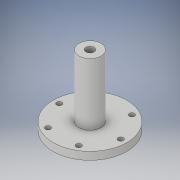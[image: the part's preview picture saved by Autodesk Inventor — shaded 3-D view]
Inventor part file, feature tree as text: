
AUTODESK INVENTOR PART (.ipt)
format: ipt  version: 2017 (Build 210142000, 142)  size: 154,624 bytes
history: native  units: in
note: dims shown in document units (in); Inventor stores cm internally (conversion verified against a paired STEP export)
features: sketch x4, hole x2, pattern_circular x2, revolve x1
ambient origin geometry x8: Origin, YZ Plane, XZ Plane, XY Plane, X Axis, Y Axis, Z Axis, Center Point
bodies: Solid1 (feature_tree)
feature tree (9):
  revolve  "Revolution1"  Angle=90.0deg
  hole  "Hole2"  [1 undecoded]
  pattern_circular  "Circular Pattern2"  Count=4 Angle=360.0deg
  sketch  "Sketch6"  dims[d42=0.104in d43=0.2in d44=0.375in d45=0.25in d46=0.5635in d47=0.2in d48=0.8108in]
  hole  "Hole3"  [1 undecoded]
  pattern_circular  "Circular Pattern3"  Count=6 Angle=360.0deg
  sketch  "Sketch1"  dims[d0=1.0394in d14=90.0deg]
  sketch  "Sketch5"  dims[d39=0.385in d40=45.0deg]
  sketch  "Sketch7"  dims[d53=1.8895in d54=1.5748in d55=360.0deg d57=0.935in d58=0.16in d59=0.75in d60=0.25in d61=0.115in d62=0.5635in d63=1.0in d64=0.8108in d65=2.3622in d66=360.0deg]
note: 2 required parameter values undecoded (feature->parameter linkage not recoverable at this tier; creation-order binding heuristic only, values carry confidence <= 0.55)
